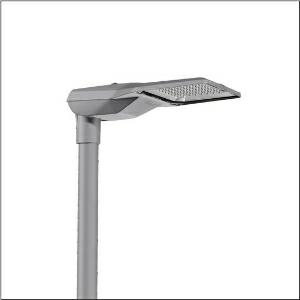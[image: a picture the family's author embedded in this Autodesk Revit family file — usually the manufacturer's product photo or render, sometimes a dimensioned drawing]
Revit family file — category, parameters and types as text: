
# Revit family: streetlight_sl_21_midi___p0_5a_5xe3v33s08nb_fb54
name_source: partatom
category: Lighting Fixtures
units: mm (PartAtom-declared; Revit-internal decimal feet)

## family parameters
Cut with Voids When Loaded = No
Host = Face
Light Source = No
Part Type = Normal
Room Calculation Point = No
Round Connector Dimension = Use Diameter
Shared = No

## types (1)
- --- (1 x LED, 22310 lm, 151.2 W, 3000K)
    Apparent Load = 151 VA
    CIE Flux Codes = 37 73 96 100 100
    Color Rendering = 70
    Color Temperature = 3000K
    Default Elevation = 1800 mm
    Description = Streetlight SL 21 midi, mast luminaire, primary light control with lens, of PMMA, primary optical cover: cover, of toughened safety glass, transparent, light distribution: P0.5a, light emission: direct distribution, primary light characteristic: asymmetric, installation type: post-top, side-entry, LED, High Power LED, rated luminous flux: 22.310lm, luminous efficacy: 148lm/W, light colour: 730, colour temperature: 3000K, control gear: D4i, control: pre-setting: logarithmic dimming characteristic, flexible luminous flux parameterisation, time-dependent luminous flux control, constant luminous flux control, overheat protection, mains connection: 230..240V, AC, 50/60Hz, start of lifetime: 151W, end of service life: 157W, reduction: 70W, luminaire housing, of diecast aluminium, powder-coated, SITECO metallic grey (DB 702S), corrosivity category C5 high according to DIN EN ISO 12944, multi-level sealing system, sealing non-destructively replaceable, inclination adjustable: 0°, 5°, 10°, 15°, please order mast flange separately, length: 644mm, width: 335mm, height: 110mm, mast flange for spigot size: 42mm (side-entry): 5XC10008XM4, 60/48mm (side-entry/post-top): 5XC10108XM2, 76/60mm (side-entry/post-top): 5XC10108XM1, mounting height: 4..8m, Smart Interface above, protection rating (complete): IP66, insulation class (complete): insulation class II (safety insulation), certification: CE, ENEC, ENEC+, VDE, impact resistance: IK10, permissible operating ambient temperature for outdoor applications: -40..+50°C, standard-compliant lighting for roads and squares, packaging unit: 1 piece

Light Distribution: P0.5a
    Height = 111 mm
    Lamp = 1 x LED
    Lamp Light Flux = 22310 lm
    Lamp Power = 151.2 W
    Lamp count = 1
    Length = 644 mm
    Luminous efficacy = 148 lm/W
    Manufacturer = Siteco
    ModVariant = No
    Model = 5XE3V33S08NB
    Number of Poles = 1
    OnlyDefault = Yes
    Power Factor = 1
    Product Name = Streetlight SL 21 midi | P0.5a
    Product group = mast luminaire | pylon top
    ProductGroupID = 6100
    Protection Class = Protection class II
    Protection Degree = IP 66
    RLX_Detail_Level = 1
    RLX_Emergency_Light_Flux = 0 lm
    RLX_Emergency_Type = 0
    RLX_Emergency_Type_DB = No
    RlxData = <blob elided: 90605 chars, md5=98b5b9f4>
    Socket = socket
    Standby Power = 0 W
    System Light Flux = 22310 lm
    System Power = 151 W
    Type Comments = factory setting: luminous flux: 100 % | dim-lin: 254 | 802 mA
    Type Image = l_1004302.jpg
    URL = http://relux.com
    VarID = @adj_076783
    Voltage = 0 V
    Weight = 0.00 kg
    Width = 336 mm

## geometry (parser evidence)
native form markers: Blend x4, Sweep x12
no freeform markers — native parametric forms only
